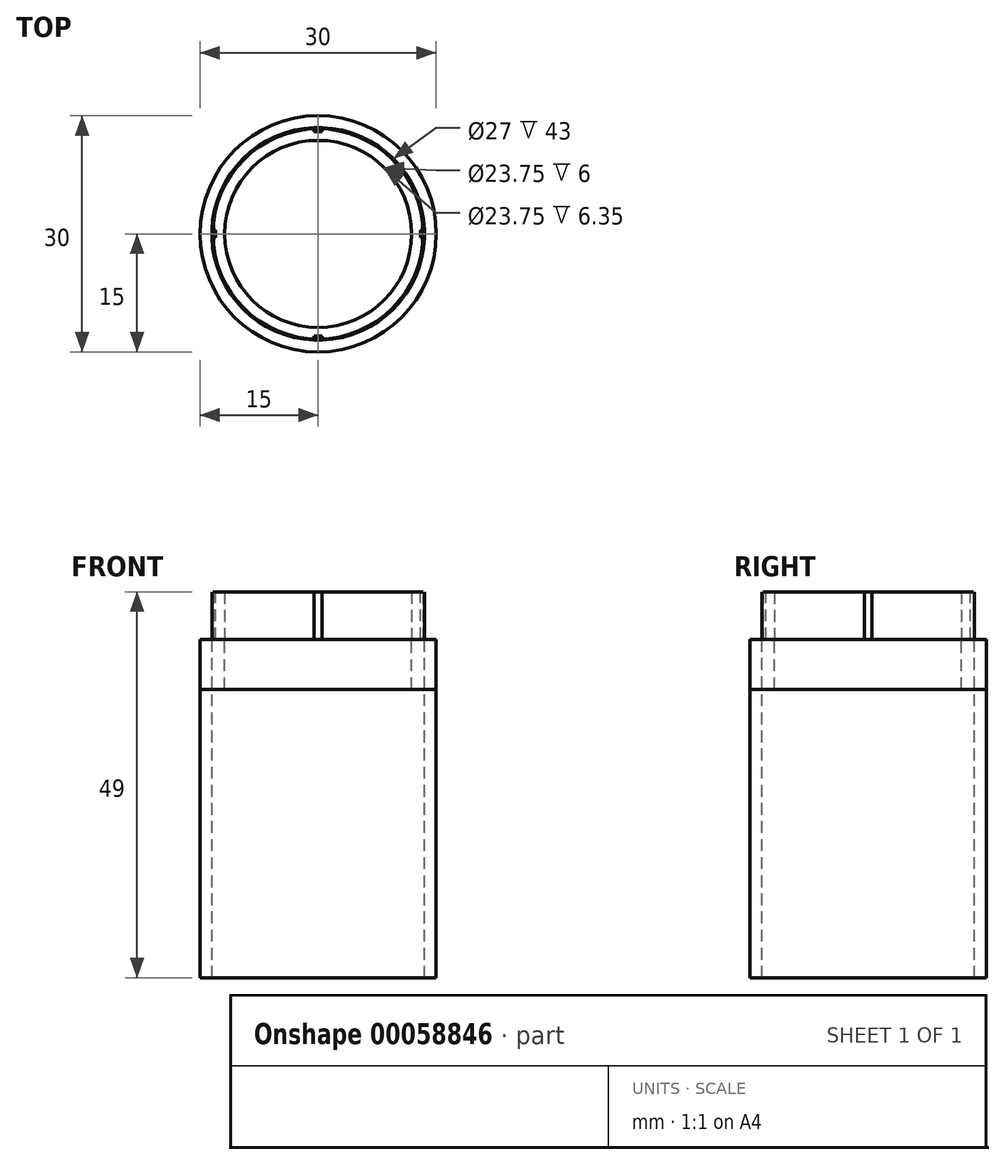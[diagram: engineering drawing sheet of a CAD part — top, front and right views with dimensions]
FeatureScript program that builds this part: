
annotation { "Feature Type Name" : "Feature", "Feature Type Description" : "" }
export const myFeature = defineFeature(function(context is Context, id is Id, definition is map)
    precondition{}
    {
        {
            var Q0;
            Q0=qCreatedBy(makeId("Top.planeOp"),FACE);
            var sketch = newSketch(context, id + "F0", { "sketchPlane" : qUnion([Q0])});
            skCircle(sketch, "E0", {"center": v(0, 0) * mm, "radius": 11.88 * mm});
            skCircle(sketch, "E1", {"center": v(0, 0) * mm, "radius": 13.35 * mm});
            skSolve(sketch);
        }
        {
            var Q0;
            Q0=qSketchRegion(id+"F0",true);
            extrude(context, id + "F1", {"entities" : qUnion([Q0]), "depth" : 6 * mm});
        }
        {
            var Q0;
            Q0=qCreatedBy(makeId("Top.planeOp"),FACE);
            var sketch = newSketch(context, id + "F2", { "sketchPlane" : qUnion([Q0])});
            skCircle(sketch, "E2", {"center": v(0, 0) * mm, "radius": 13.5 * mm});
            skCircle(sketch, "E3", {"center": v(0, 0) * mm, "radius": 15 * mm});
            skSolve(sketch);
        }
        {
            var Q0;
            Q0=qSketchRegion(id+"F2",true);
            extrude(context, id + "F3", {"entities" : qUnion([Q0]), "operationType" : NewBodyOperationType.ADD, "oppositeDirection" : true, "depth" : 43 * mm});
        }
        {
            var Q0;
            Q0=qCreatedBy(makeId("Top.planeOp"),FACE);
            var sketch = newSketch(context, id + "F4", { "sketchPlane" : qUnion([Q0])});
            skCircle(sketch, "E4", {"center": v(0, 0) * mm, "radius": 11.88 * mm});
            skCircle(sketch, "E5", {"center": v(0, 0) * mm, "radius": 15 * mm});
            skSolve(sketch);
        }
        {
            var Q0;
            Q0=qSketchRegion(id+"F4",true);
            extrude(context, id + "F5", {"entities" : qUnion([Q0]), "oppositeDirection" : true, "depth" : 6.35 * mm});
        }
        {
            var Q0;
            Q0=qCreatedBy(makeId("Right.planeOp"),FACE);
            cPlane(context, id + "F6", {"entities" : qUnion([Q0]), "cplaneType" : CPlaneType.OFFSET, "offset" : 13 * mm, "width" : 152.4 * mm, "height" : 152.4 * mm});
        }
        {
            var Q0;
            Q0=qCreatedBy(id+"F6.planeOp",FACE);
            var sketch = newSketch(context, id + "F7", { "sketchPlane" : qUnion([Q0])});
            skLineSegment(sketch, "E6.bottom", {"start": v(-0.5, 0) * mm, "end": v(0.5, 0) * mm});
            skLineSegment(sketch, "E6.top", {"start": v(-0.5, 6) * mm, "end": v(0.5, 6) * mm});
            skLineSegment(sketch, "E6.left", {"start": v(-0.5, 0) * mm, "end": v(-0.5, 6) * mm});
            skLineSegment(sketch, "E6.right", {"start": v(0.5, 0) * mm, "end": v(0.5, 6) * mm});
            skSolve(sketch);
        }
        {
            var Q0;
            Q0=qSketchRegion(id+"F7",true);
            extrude(context, id + "F8", {"entities" : qUnion([Q0]), "depth" : 0.5 * mm});
        }
        {
            var Q0;
            Q0=qCreatedBy(makeId("Right.planeOp"),FACE);
            cPlane(context, id + "F9", {"entities" : qUnion([Q0]), "cplaneType" : CPlaneType.OFFSET, "offset" : 13 * mm, "oppositeDirection" : true, "width" : 152.4 * mm, "height" : 152.4 * mm});
        }
        {
            var Q0;
            Q0=qCreatedBy(id+"F9.planeOp",FACE);
            var sketch = newSketch(context, id + "F10", { "sketchPlane" : qUnion([Q0])});
            skLineSegment(sketch, "E7.bottom", {"start": v(-0.5, 0) * mm, "end": v(0.5, 0) * mm});
            skLineSegment(sketch, "E7.top", {"start": v(-0.5, 6) * mm, "end": v(0.5, 6) * mm});
            skLineSegment(sketch, "E7.left", {"start": v(-0.5, 0) * mm, "end": v(-0.5, 6) * mm});
            skLineSegment(sketch, "E7.right", {"start": v(0.5, 0) * mm, "end": v(0.5, 6) * mm});
            skSolve(sketch);
        }
        {
            var Q0;
            Q0=qSketchRegion(id+"F10",true);
            extrude(context, id + "F11", {"entities" : qUnion([Q0]), "oppositeDirection" : true, "depth" : 0.5 * mm});
        }
        {
            var Q0;
            Q0=qCreatedBy(makeId("Front.planeOp"),FACE);
            cPlane(context, id + "F12", {"entities" : qUnion([Q0]), "cplaneType" : CPlaneType.OFFSET, "offset" : 13 * mm, "oppositeDirection" : true, "width" : 152.4 * mm, "height" : 152.4 * mm});
        }
        {
            var Q0;
            Q0=qCreatedBy(id+"F12.planeOp",FACE);
            var sketch = newSketch(context, id + "F13", { "sketchPlane" : qUnion([Q0])});
            skLineSegment(sketch, "E8.bottom", {"start": v(0.5, 0) * mm, "end": v(-0.5, 0) * mm});
            skLineSegment(sketch, "E8.top", {"start": v(0.5, 6) * mm, "end": v(-0.5, 6) * mm});
            skLineSegment(sketch, "E8.left", {"start": v(0.5, 0) * mm, "end": v(0.5, 6) * mm});
            skLineSegment(sketch, "E8.right", {"start": v(-0.5, 0) * mm, "end": v(-0.5, 6) * mm});
            skSolve(sketch);
        }
        {
            var Q0;
            Q0=qSketchRegion(id+"F13",true);
            extrude(context, id + "F14", {"entities" : qUnion([Q0]), "oppositeDirection" : true, "depth" : 0.5 * mm});
        }
        {
            var Q0;
            Q0=qCreatedBy(makeId("Front.planeOp"),FACE);
            cPlane(context, id + "F15", {"entities" : qUnion([Q0]), "cplaneType" : CPlaneType.OFFSET, "offset" : 13 * mm, "width" : 152.4 * mm, "height" : 152.4 * mm});
        }
        {
            var Q0;
            Q0=qCreatedBy(id+"F15.planeOp",FACE);
            var sketch = newSketch(context, id + "F16", { "sketchPlane" : qUnion([Q0])});
            skLineSegment(sketch, "E9.bottom", {"start": v(-0.5, 0) * mm, "end": v(0.5, 0) * mm});
            skLineSegment(sketch, "E9.top", {"start": v(-0.5, 6) * mm, "end": v(0.5, 6) * mm});
            skLineSegment(sketch, "E9.left", {"start": v(-0.5, 0) * mm, "end": v(-0.5, 6) * mm});
            skLineSegment(sketch, "E9.right", {"start": v(0.5, 0) * mm, "end": v(0.5, 6) * mm});
            skSolve(sketch);
        }
        {
            var Q0;
            Q0=qSketchRegion(id+"F16",true);
            extrude(context, id + "F17", {"entities" : qUnion([Q0]), "depth" : 0.5 * mm});
        }
    });
